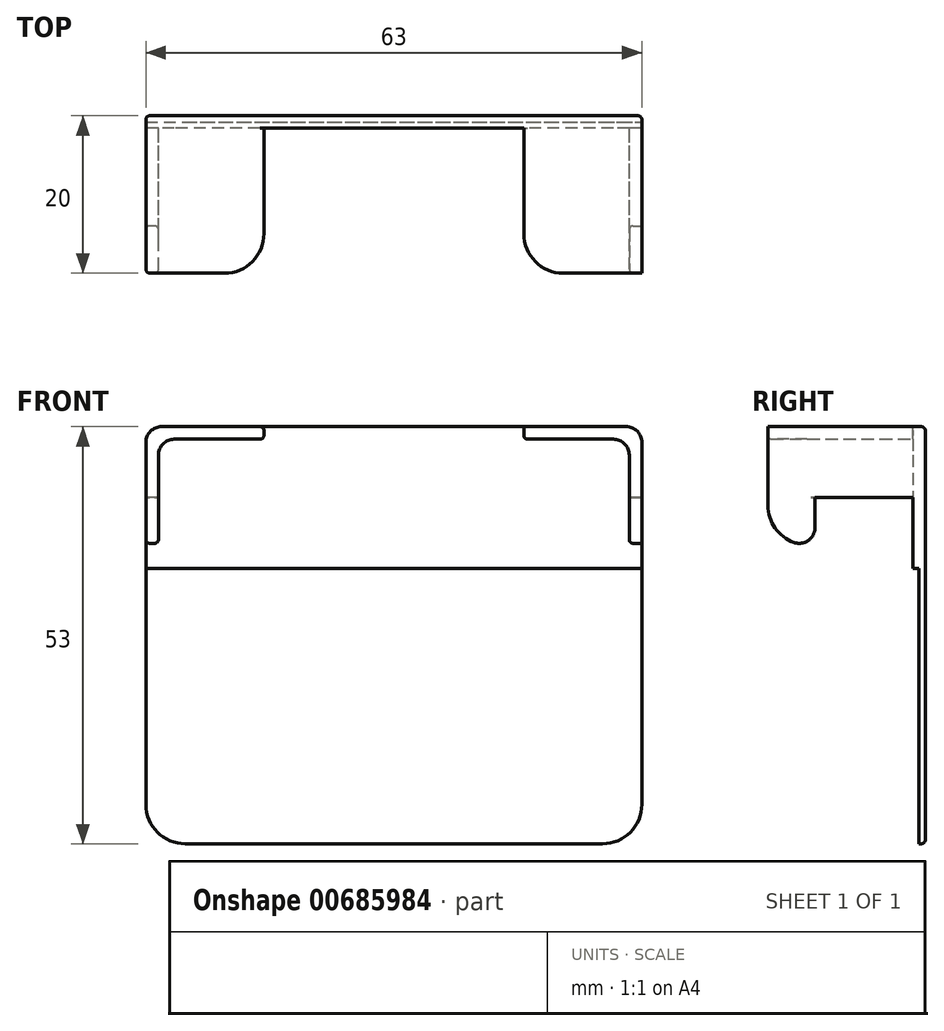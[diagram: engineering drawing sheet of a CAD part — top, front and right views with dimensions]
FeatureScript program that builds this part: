
annotation { "Feature Type Name" : "Feature", "Feature Type Description" : "" }
export const myFeature = defineFeature(function(context is Context, id is Id, definition is map)
    precondition{}
    {
        {
            var Q0;
            Q0=qCreatedBy(makeId("Front.planeOp"),FACE);
            var sketch = newSketch(context, id + "F0", { "sketchPlane" : qUnion([Q0])});
            skLineSegment(sketch, "E0.bottom", {"start": v(0, 53) * mm, "end": v(63, 53) * mm});
            skLineSegment(sketch, "E0.top", {"start": v(0, 0) * mm, "end": v(63, 0) * mm});
            skLineSegment(sketch, "E0.left", {"start": v(0, 53) * mm, "end": v(0, 0) * mm});
            skLineSegment(sketch, "E0.right", {"start": v(63, 53) * mm, "end": v(63, 0) * mm});
            skSolve(sketch);
        }
        {
            var Q0;
            Q0=makeQuery(id+"F0.imprint","IMPRINT",FACE,{"disambiguationData":[TD([[makeQuery(id+"F0.imprint","IMPRINT",EDGE,{"derivedFrom":sQuery(id+"F0.wireOp",EDGE,"E0.bottom")}),-1.0]])]});
            extrude(context, id + "F1", {"entities" : qUnion([Q0]), "depth" : 0.8 * mm, "offsetDistance" : 25 * mm});
        }
        {
            var Q0;
            Q0=makeQuery(id+"F1.opExtrude","CAP_FACE",FACE,{"disambiguationData":[OSD([sQuery(id+"F0.wireOp",EDGE,"E0.bottom"),sQuery(id+"F0.wireOp",EDGE,"E0.top"),sQuery(id+"F0.wireOp",EDGE,"E0.left"),sQuery(id+"F0.wireOp",EDGE,"E0.right")])],"isStart":false});
            var sketch = newSketch(context, id + "F2", { "sketchPlane" : qUnion([Q0])});
            skLineSegment(sketch, "E1.bottom", {"start": v(0, 53) * mm, "end": v(63, 53) * mm});
            skLineSegment(sketch, "E1.top", {"start": v(0, 35) * mm, "end": v(63, 35) * mm});
            skLineSegment(sketch, "E1.left", {"start": v(0, 53) * mm, "end": v(0, 35) * mm});
            skLineSegment(sketch, "E1.right", {"start": v(63, 53) * mm, "end": v(63, 35) * mm});
            skSolve(sketch);
        }
        {
            var Q0;
            Q0=makeQuery(id+"F2.imprint","IMPRINT",FACE,{"disambiguationData":[TD([[makeQuery(id+"F2.imprint","IMPRINT",EDGE,{"derivedFrom":sQuery(id+"F2.wireOp",EDGE,"E1.bottom")}),-1.0]])]});
            extrude(context, id + "F3", {"entities" : qUnion([Q0]), "operationType" : NewBodyOperationType.ADD, "depth" : 0.8 * mm, "offsetDistance" : 25 * mm});
        }
        {
            var Q0;
            Q0=makeQuery(id+"F3.opExtrude","CAP_FACE",FACE,{"disambiguationData":[OSD([sQuery(id+"F2.wireOp",EDGE,"E1.bottom"),sQuery(id+"F2.wireOp",EDGE,"E1.top"),sQuery(id+"F2.wireOp",EDGE,"E1.left"),sQuery(id+"F2.wireOp",EDGE,"E1.right")])],"isStart":false});
            var sketch = newSketch(context, id + "F4", { "sketchPlane" : qUnion([Q0])});
            skLineSegment(sketch, "E2", {"start": v(0, 44) * mm, "end": v(0, 53) * mm});
            skLineSegment(sketch, "E3", {"start": v(0, 53) * mm, "end": v(15, 53) * mm});
            skLineSegment(sketch, "E4", {"start": v(63, 53) * mm, "end": v(63, 44) * mm});
            skLineSegment(sketch, "E5", {"start": v(63, 44) * mm, "end": v(61.4, 44) * mm});
            skLineSegment(sketch, "E6", {"start": v(61.4, 44) * mm, "end": v(61.4, 51.4) * mm});
            skLineSegment(sketch, "E7", {"start": v(61.4, 51.4) * mm, "end": v(48, 51.4) * mm});
            skLineSegment(sketch, "E8", {"start": v(1.6, 51.4) * mm, "end": v(1.6, 44) * mm});
            skLineSegment(sketch, "E9", {"start": v(1.6, 44) * mm, "end": v(0, 44) * mm});
            skLineSegment(sketch, "E10", {"start": v(15, 53) * mm, "end": v(15, 51.4) * mm});
            skLineSegment(sketch, "E11", {"start": v(48, 51.4) * mm, "end": v(48, 53) * mm});
            skLineSegment(sketch, "E12.trimOffspring", {"start": v(48, 53) * mm, "end": v(63, 53) * mm});
            skLineSegment(sketch, "E13.trimOffspring", {"start": v(15, 51.4) * mm, "end": v(1.6, 51.4) * mm});
            skSolve(sketch);
        }
        {
            var Q0;
            Q0=makeQuery(id+"F4.imprint","IMPRINT",FACE,{"disambiguationData":[TD([[makeQuery(id+"F4.imprint","IMPRINT",EDGE,{"derivedFrom":sQuery(id+"F4.wireOp",EDGE,"E4")}),-1.0]])]});
            var Q1;
            Q1=makeQuery(id+"F4.imprint","IMPRINT",FACE,{"disambiguationData":[TD([[makeQuery(id+"F4.imprint","IMPRINT",EDGE,{"derivedFrom":sQuery(id+"F4.wireOp",EDGE,"E2")}),1.0]])]});
            extrude(context, id + "F5", {"entities" : qUnion([Q0, Q1]), "operationType" : NewBodyOperationType.ADD, "depth" : 18.4 * mm, "offsetDistance" : 25 * mm});
        }
        {
            var Q0;
            Q0=makeQuery(id+"F5.opExtrude","SWEPT_FACE",FACE,{"disambiguationData":[OSD([sQuery(id+"F4.wireOp",EDGE,"E9")])]});
            var sketch = newSketch(context, id + "F6", { "sketchPlane" : qUnion([Q0])});
            skLineSegment(sketch, "E14.bottom", {"start": v(1.6, 14) * mm, "end": v(0, 14) * mm});
            skLineSegment(sketch, "E14.top", {"start": v(1.6, 20) * mm, "end": v(0, 20) * mm});
            skLineSegment(sketch, "E14.left", {"start": v(1.6, 14) * mm, "end": v(1.6, 20) * mm});
            skLineSegment(sketch, "E14.right", {"start": v(0, 14) * mm, "end": v(0, 20) * mm});
            skLineSegment(sketch, "E15.bottom", {"start": v(61.4, 20) * mm, "end": v(63, 20) * mm});
            skLineSegment(sketch, "E15.top", {"start": v(61.4, 14) * mm, "end": v(63, 14) * mm});
            skLineSegment(sketch, "E15.left", {"start": v(61.4, 20) * mm, "end": v(61.4, 14) * mm});
            skLineSegment(sketch, "E15.right", {"start": v(63, 20) * mm, "end": v(63, 14) * mm});
            skSolve(sketch);
        }
        {
            var Q0;
            Q0=makeQuery(id+"F6.imprint","IMPRINT",FACE,{"disambiguationData":[TD([[makeQuery(id+"F6.imprint","IMPRINT",EDGE,{"derivedFrom":sQuery(id+"F6.wireOp",EDGE,"E14.bottom")}),-1.0]])]});
            var Q1;
            Q1=makeQuery(id+"F6.imprint","IMPRINT",FACE,{"disambiguationData":[TD([[makeQuery(id+"F6.imprint","IMPRINT",EDGE,{"derivedFrom":sQuery(id+"F6.wireOp",EDGE,"E15.bottom")}),-1.0]])]});
            extrude(context, id + "F7", {"entities" : qUnion([Q0, Q1]), "operationType" : NewBodyOperationType.ADD, "depth" : 6 * mm, "offsetDistance" : 25 * mm});
        }
        {
            var Q0;
            Q0=makeQuery(id+"F1.opExtrude","SWEPT_EDGE",EDGE,{"disambiguationData":[OSD([sQuery(id+"F0.wireOp",EDGE,"E0.top"),sQuery(id+"F0.wireOp",EDGE,"E0.left")])]});
            var Q1;
            Q1=makeQuery(id+"F1.opExtrude","SWEPT_EDGE",EDGE,{"disambiguationData":[OSD([sQuery(id+"F0.wireOp",EDGE,"E0.top"),sQuery(id+"F0.wireOp",EDGE,"E0.right")])]});
            var Q2;
            Q2=makeQuery(id+"F5.opExtrude","CAP_EDGE",EDGE,{"disambiguationData":[OSD([sQuery(id+"F4.wireOp",EDGE,"E11")])],"isStart":false});
            var Q3;
            Q3=makeQuery(id+"F5.opExtrude","CAP_EDGE",EDGE,{"disambiguationData":[OSD([sQuery(id+"F4.wireOp",EDGE,"E11")])],"isStart":true});
            var Q4;
            Q4=makeQuery(id+"F5.opExtrude","CAP_EDGE",EDGE,{"disambiguationData":[OSD([sQuery(id+"F4.wireOp",EDGE,"E10")])],"isStart":false});
            var Q5;
            Q5=makeQuery(id+"F5.opExtrude","CAP_EDGE",EDGE,{"disambiguationData":[OSD([sQuery(id+"F4.wireOp",EDGE,"E10")])],"isStart":true});
            var Q6;
            Q6=makeQuery(id+"F5.opExtrude","CAP_EDGE",EDGE,{"disambiguationData":[OSD([sQuery(id+"F4.wireOp",EDGE,"E9")])],"isStart":true});
            var Q7;
            Q7=makeQuery(id+"F7.opExtrude","CAP_EDGE",EDGE,{"disambiguationData":[OSD([sQuery(id+"F6.wireOp",EDGE,"E14.top")])],"isStart":false});
            var Q8;
            Q8=makeQuery(id+"F5.opExtrude","CAP_EDGE",EDGE,{"disambiguationData":[OSD([sQuery(id+"F4.wireOp",EDGE,"E5")])],"isStart":true});
            var Q9;
            Q9=makeQuery(id+"F7.opExtrude","CAP_EDGE",EDGE,{"disambiguationData":[OSD([sQuery(id+"F6.wireOp",EDGE,"E15.bottom")])],"isStart":false});
            var Q10;
            Q10=makeQuery(id+"F7.opExtrude","CAP_EDGE",EDGE,{"disambiguationData":[OSD([sQuery(id+"F6.wireOp",EDGE,"E14.bottom")])],"isStart":true});
            var Q11;
            Q11=makeQuery(id+"F7.opExtrude","CAP_EDGE",EDGE,{"disambiguationData":[OSD([sQuery(id+"F6.wireOp",EDGE,"E15.top")])],"isStart":true});
            fillet(context, id + "F8", {"entities" : qUnion([Q0, Q1, Q2, Q3, Q4, Q5, Q6, Q7, Q8, Q9, Q10, Q11]), "radius" : 5 * mm, "tangentPropagation" : true, "allowEdgeOverflow" : false});
        }
        {
            var Q0;
            Q0=makeQuery(id+"F7.opExtrude","CAP_EDGE",EDGE,{"disambiguationData":[OSD([sQuery(id+"F6.wireOp",EDGE,"E15.top")])],"isStart":false});
            var Q1;
            Q1=makeQuery(id+"F7.opExtrude","CAP_EDGE",EDGE,{"disambiguationData":[OSD([sQuery(id+"F6.wireOp",EDGE,"E14.bottom")])],"isStart":false});
            var Q2;
            Q2=makeQuery(id+"F5.opExtrude","SWEPT_EDGE",EDGE,{"disambiguationData":[OSD([sQuery(id+"F4.wireOp",EDGE,"E6"),sQuery(id+"F4.wireOp",EDGE,"E7")])]});
            var Q3;
            Q3=makeQuery(id+"F5.opExtrude","SWEPT_EDGE",EDGE,{"disambiguationData":[OSD([sQuery(id+"F4.wireOp",EDGE,"E8"),sQuery(id+"F4.wireOp",EDGE,"E13.trimOffspring")])]});
            var Q4;
            Q4=makeQuery(id+"F5.boolean.opBoolean","MERGE",EDGE,{"derivedFrom":[makeQuery(id+"F3.boolean.opBoolean","MERGE",EDGE,{"derivedFrom":[makeQuery(id+"F1.opExtrude","SWEPT_EDGE",EDGE,{"disambiguationData":[OSD([sQuery(id+"F0.wireOp",EDGE,"E0.bottom"),sQuery(id+"F0.wireOp",EDGE,"E0.right")])]}),makeQuery(id+"F3.opExtrude","SWEPT_EDGE",EDGE,{"disambiguationData":[OSD([sQuery(id+"F2.wireOp",EDGE,"E1.bottom"),sQuery(id+"F2.wireOp",EDGE,"E1.right")])]})]}),makeQuery(id+"F5.opExtrude","SWEPT_EDGE",EDGE,{"disambiguationData":[OSD([sQuery(id+"F4.wireOp",EDGE,"E4"),sQuery(id+"F4.wireOp",EDGE,"E12.trimOffspring")])]})]});
            var Q5;
            Q5=makeQuery(id+"F5.boolean.opBoolean","MERGE",EDGE,{"derivedFrom":[makeQuery(id+"F3.boolean.opBoolean","MERGE",EDGE,{"derivedFrom":[makeQuery(id+"F1.opExtrude","SWEPT_EDGE",EDGE,{"disambiguationData":[OSD([sQuery(id+"F0.wireOp",EDGE,"E0.bottom"),sQuery(id+"F0.wireOp",EDGE,"E0.left")])]}),makeQuery(id+"F3.opExtrude","SWEPT_EDGE",EDGE,{"disambiguationData":[OSD([sQuery(id+"F2.wireOp",EDGE,"E1.bottom"),sQuery(id+"F2.wireOp",EDGE,"E1.left")])]})]}),makeQuery(id+"F5.opExtrude","SWEPT_EDGE",EDGE,{"disambiguationData":[OSD([sQuery(id+"F4.wireOp",EDGE,"E2"),sQuery(id+"F4.wireOp",EDGE,"E3")])]})]});
            fillet(context, id + "F9", {"entities" : qUnion([Q0, Q1, Q2, Q3, Q4, Q5]), "radius" : 2 * mm, "tangentPropagation" : true, "allowEdgeOverflow" : false});
        }
        {
            var Q0;
            {var subQ0=sQuery(id+"F4.wireOp",EDGE,"E3");var subQ1=sQuery(id+"F4.wireOp",EDGE,"E2");Q0=makeQuery(id+"F9.opFillet","BLEND_EDGE",EDGE,{"blendedFrom":[makeQuery(id+"F5.boolean.opBoolean","MERGE",EDGE,{"derivedFrom":[makeQuery(id+"F3.boolean.opBoolean","MERGE",EDGE,{"derivedFrom":[makeQuery(id+"F1.opExtrude","SWEPT_EDGE",EDGE,{"disambiguationData":[OSD([sQuery(id+"F0.wireOp",EDGE,"E0.bottom"),sQuery(id+"F0.wireOp",EDGE,"E0.left")])]}),makeQuery(id+"F3.opExtrude","SWEPT_EDGE",EDGE,{"disambiguationData":[OSD([sQuery(id+"F2.wireOp",EDGE,"E1.bottom"),sQuery(id+"F2.wireOp",EDGE,"E1.left")])]})]}),makeQuery(id+"F5.opExtrude","SWEPT_EDGE",EDGE,{"disambiguationData":[OSD([subQ1,subQ0])]})]}),makeQuery(id+"F7.boolean.opBoolean","MERGE",FACE,{"derivedFrom":[makeQuery(id+"F5.opExtrude","CAP_FACE",FACE,{"disambiguationData":[OSD([subQ1,subQ0,sQuery(id+"F4.wireOp",EDGE,"E8"),sQuery(id+"F4.wireOp",EDGE,"E9"),sQuery(id+"F4.wireOp",EDGE,"E10"),sQuery(id+"F4.wireOp",EDGE,"E13.trimOffspring")])],"isStart":false}),makeQuery(id+"F7.opExtrude","SWEPT_FACE",FACE,{"disambiguationData":[OSD([sQuery(id+"F6.wireOp",EDGE,"E14.top")])]})]})],"blendedInto":[makeQuery(id+"F7.boolean.opBoolean","MERGE",FACE,{"derivedFrom":[makeQuery(id+"F5.opExtrude","CAP_FACE",FACE,{"disambiguationData":[OSD([subQ1,subQ0,sQuery(id+"F4.wireOp",EDGE,"E8"),sQuery(id+"F4.wireOp",EDGE,"E9"),sQuery(id+"F4.wireOp",EDGE,"E10"),sQuery(id+"F4.wireOp",EDGE,"E13.trimOffspring")])],"isStart":false}),makeQuery(id+"F7.opExtrude","SWEPT_FACE",FACE,{"disambiguationData":[OSD([sQuery(id+"F6.wireOp",EDGE,"E14.top")])]})]})]});}
            var Q1;
            Q1=makeQuery(id+"F8.opFillet","BLEND_EDGE",EDGE,{"blendedFrom":[makeQuery(id+"F7.opExtrude","CAP_EDGE",EDGE,{"disambiguationData":[OSD([sQuery(id+"F6.wireOp",EDGE,"E15.bottom")])],"isStart":false}),makeQuery(id+"F7.boolean.opBoolean","MERGE",FACE,{"derivedFrom":[makeQuery(id+"F5.opExtrude","SWEPT_FACE",FACE,{"disambiguationData":[OSD([sQuery(id+"F4.wireOp",EDGE,"E6")])]}),makeQuery(id+"F7.opExtrude","SWEPT_FACE",FACE,{"disambiguationData":[OSD([sQuery(id+"F6.wireOp",EDGE,"E15.left")])]})]})],"blendedInto":[makeQuery(id+"F7.boolean.opBoolean","MERGE",FACE,{"derivedFrom":[makeQuery(id+"F5.opExtrude","SWEPT_FACE",FACE,{"disambiguationData":[OSD([sQuery(id+"F4.wireOp",EDGE,"E6")])]}),makeQuery(id+"F7.opExtrude","SWEPT_FACE",FACE,{"disambiguationData":[OSD([sQuery(id+"F6.wireOp",EDGE,"E15.left")])]})]})]});
            var Q2;
            Q2=makeQuery(id+"F8.opFillet","BLEND_EDGE",EDGE,{"blendedFrom":[makeQuery(id+"F7.opExtrude","CAP_EDGE",EDGE,{"disambiguationData":[OSD([sQuery(id+"F6.wireOp",EDGE,"E14.top")])],"isStart":false}),makeQuery(id+"F7.boolean.opBoolean","MERGE",FACE,{"derivedFrom":[makeQuery(id+"F5.opExtrude","SWEPT_FACE",FACE,{"disambiguationData":[OSD([sQuery(id+"F4.wireOp",EDGE,"E8")])]}),makeQuery(id+"F7.opExtrude","SWEPT_FACE",FACE,{"disambiguationData":[OSD([sQuery(id+"F6.wireOp",EDGE,"E14.left")])]})]})],"blendedInto":[makeQuery(id+"F7.boolean.opBoolean","MERGE",FACE,{"derivedFrom":[makeQuery(id+"F5.opExtrude","SWEPT_FACE",FACE,{"disambiguationData":[OSD([sQuery(id+"F4.wireOp",EDGE,"E8")])]}),makeQuery(id+"F7.opExtrude","SWEPT_FACE",FACE,{"disambiguationData":[OSD([sQuery(id+"F6.wireOp",EDGE,"E14.left")])]})]})]});
            var Q3;
            Q3=makeQuery(id+"F1.opExtrude","CAP_EDGE",EDGE,{"disambiguationData":[OSD([sQuery(id+"F0.wireOp",EDGE,"E0.bottom")])],"isStart":true});
            fillet(context, id + "F10", {"entities" : qUnion([Q0, Q1, Q2, Q3]), "radius" : 0.5 * mm, "tangentPropagation" : true, "allowEdgeOverflow" : false});
        }
    });
